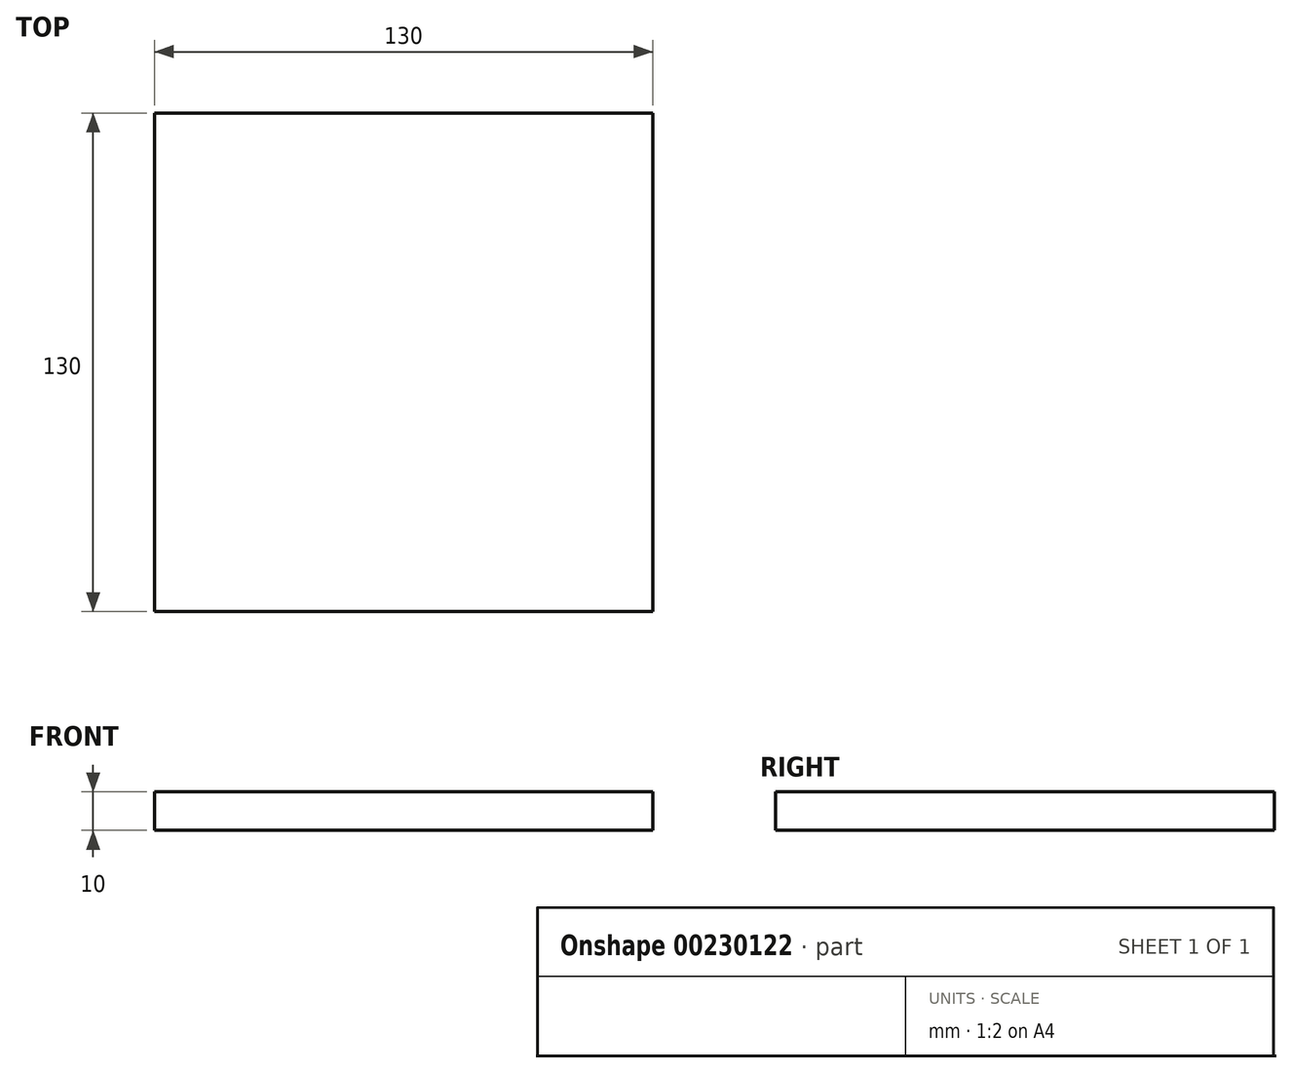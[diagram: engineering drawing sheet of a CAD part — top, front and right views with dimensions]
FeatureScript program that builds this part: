
annotation { "Feature Type Name" : "Feature", "Feature Type Description" : "" }
export const myFeature = defineFeature(function(context is Context, id is Id, definition is map)
    precondition{}
    {
        {
            var Q0;
            Q0=qCreatedBy(makeId("Top.planeOp"),FACE);
            var sketch = newSketch(context, id + "F0", { "sketchPlane" : qUnion([Q0])});
            skLineSegment(sketch, "E0.bottom", {"start": v(-65, 65) * mm, "end": v(65, 65) * mm});
            skLineSegment(sketch, "E0.top", {"start": v(-65, -65) * mm, "end": v(65, -65) * mm});
            skLineSegment(sketch, "E0.left", {"start": v(-65, 65) * mm, "end": v(-65, -65) * mm});
            skLineSegment(sketch, "E0.right", {"start": v(65, 65) * mm, "end": v(65, -65) * mm});
            skPoint(sketch, "E0.middle", {"position": v(0, 0) * mm});
            skSolve(sketch);
        }
        {
            var Q0;
            Q0 = qSketchRegion(id + "F0", true);
            extrude(context, id + "F1", {"entities" : qUnion([Q0]), "depth" : 10 * mm});
        }
    });
